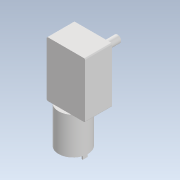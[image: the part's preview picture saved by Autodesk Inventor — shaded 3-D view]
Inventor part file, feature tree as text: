
AUTODESK INVENTOR PART (.ipt)
format: ipt  version: 2020.2 (Build 242310000, 310)  size: 188,928 bytes
history: native  units: mm
features: extrude x7, sketch x7
ambient origin geometry x8: Origin, YZ Plane, XZ Plane, XY Plane, X Axis, Y Axis, Z Axis, Center Point
bodies: Solid1 (feature_tree)
feature tree (14):
  extrude  "Extrusion1"  Depth=46.0mm
  extrude  "Extrusion2"  Depth=1.0mm
  extrude  "Extrusion3"  Depth=10.0mm
  extrude  "Extrusion4"  Depth=33.0mm
  extrude  "Extrusion5"  Depth=7.4mm
  extrude  "Extrusion6"  Depth=18.0mm
  extrude  "Extrusion7"  Depth=13.2mm
  sketch  "Sketch1"  dims[d0=16.0mm d1=46.0mm]
  sketch  "Sketch2"  dims[d2=32.0mm d3=1.0mm]
  sketch  "Sketch3"  dims[d4=22.5mm d5=0.0mm d6=10.0mm]
  sketch  "Sketch4"  dims[d7=7.0mm d8=33.0mm]
  sketch  "Sketch5"  dims[d9=7.4mm d10=7.4mm]
  sketch  "Sketch6"  dims[d11=18.0mm d12=18.0mm]
  sketch  "Sketch7"  dims[d13=7.4mm d14=7.4mm d15=2.0mm d16=0.0mm d17=3.0mm d18=3.0mm d19=3.0mm d20=3.0mm d21=3.0mm d22=0.0mm d23=15.0mm d24=12.0mm d25=6.0mm d26=18.5mm d27=0.0mm d28=5.4mm d29=10.0mm d30=0.0mm d31=24.4mm d32=30.8mm d33=0.0mm d34=10.0mm d35=2.0mm d36=4.0mm d37=1.0mm d38=4.2mm d39=0.0mm d40=13.2mm d41=12.8mm]
